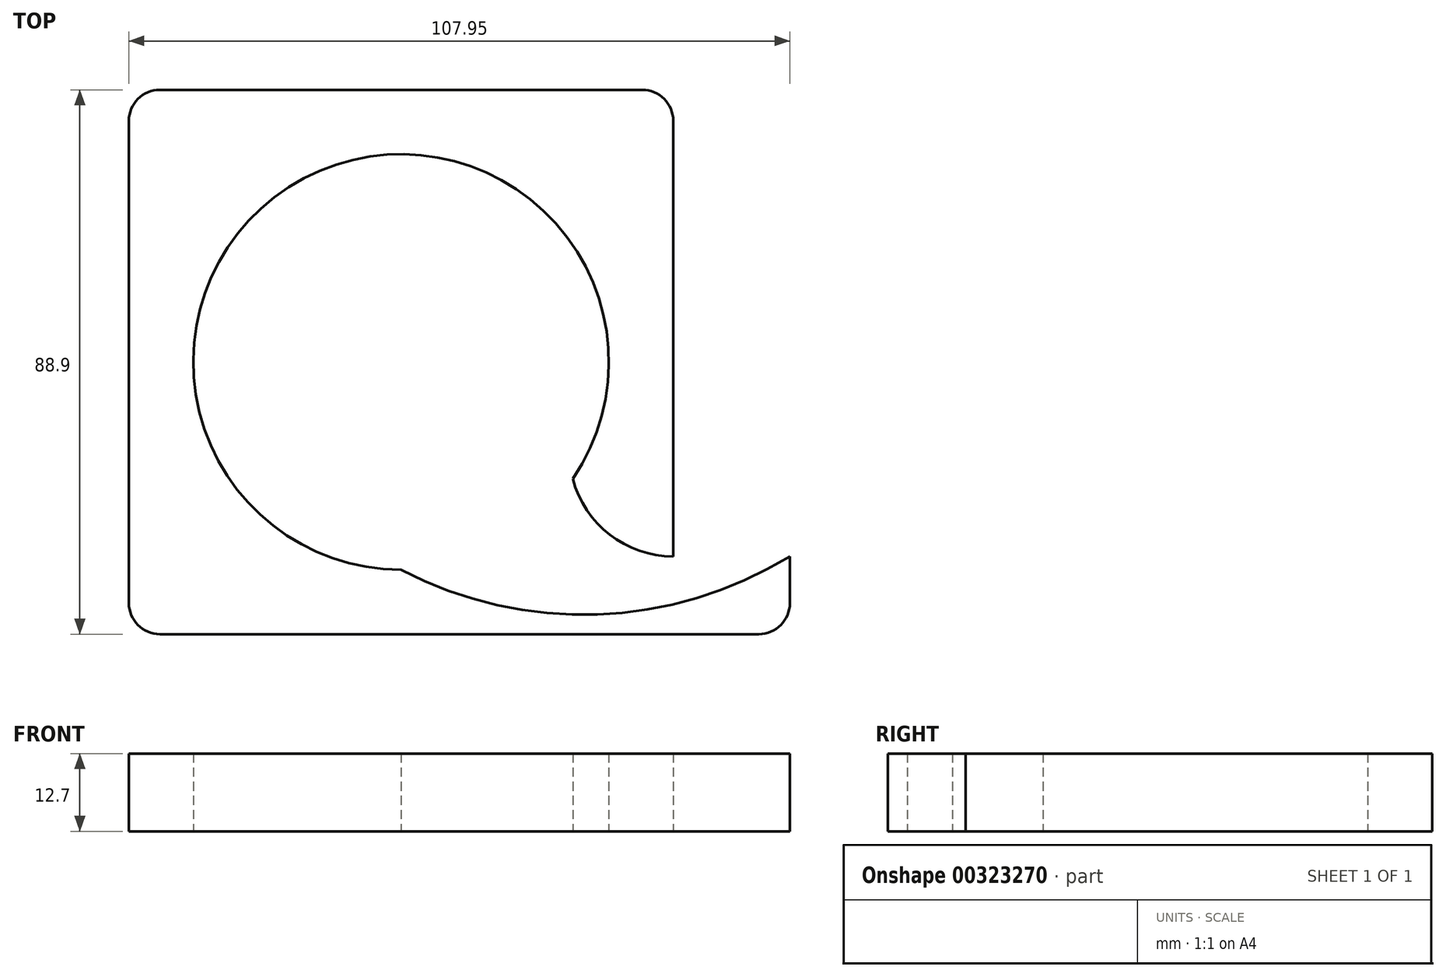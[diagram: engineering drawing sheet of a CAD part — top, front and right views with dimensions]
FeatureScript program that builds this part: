
annotation { "Feature Type Name" : "Feature", "Feature Type Description" : "" }
export const myFeature = defineFeature(function(context is Context, id is Id, definition is map)
    precondition{}
    {
        {
            var Q0;
            Q0=qCreatedBy(makeId("Top.planeOp"),FACE);
            var sketch = newSketch(context, id + "F0", { "sketchPlane" : qUnion([Q0])});
            skLineSegment(sketch, "E0.bottom", {"start": v(-44.45, 44.45) * mm, "end": v(44.45, 44.45) * mm});
            skLineSegment(sketch, "E0.top", {"start": v(-44.45, -44.45) * mm, "end": v(44.45, -44.45) * mm});
            skLineSegment(sketch, "E0.left", {"start": v(-44.45, 44.45) * mm, "end": v(-44.45, -44.45) * mm});
            skLineSegment(sketch, "E0.right", {"start": v(44.45, 44.45) * mm, "end": v(44.45, -31.75) * mm});
            skPoint(sketch, "E0.middle", {"position": v(0, 0) * mm});
            skLineSegment(sketch, "E1.bottom", {"start": v(44.45, -44.45) * mm, "end": v(63.5, -44.45) * mm});
            skLineSegment(sketch, "E1.right", {"start": v(63.5, -44.45) * mm, "end": v(63.5, -31.75) * mm});
            skArc(sketch, "E2", {"start": v(28.04, -19.1) * mm, "mid": v(-15.86, 30) * mm, "end": v(0, -33.93) * mm});
            skArc(sketch, "E3", {"start": v(0, -33.93) * mm, "mid": v(32.04, -41.23) * mm, "end": v(63.5, -31.75) * mm});
            skArc(sketch, "E4", {"start": v(28.04, -19.1) * mm, "mid": v(34.1, -28.22) * mm, "end": v(44.45, -31.75) * mm});
            skSolve(sketch);
        }
        {
            var Q0;
            Q0=makeQuery(id+"F0.imprint","IMPRINT",FACE,{"disambiguationData":[TD([[makeQuery(id+"F0.imprint","IMPRINT",EDGE,{"derivedFrom":sQuery(id+"F0.wireOp",EDGE,"E0.bottom")}),-1.0]])]});
            extrude(context, id + "F1", {"entities" : qUnion([Q0]), "depth" : 12.7 * mm});
        }
        {
            var Q0;
            Q0=makeQuery(id+"F1.opExtrude","SWEPT_EDGE",EDGE,{"disambiguationData":[OSD([sQuery(id+"F0.wireOp",EDGE,"E0.top"),sQuery(id+"F0.wireOp",EDGE,"E0.left")])]});
            var Q1;
            Q1=makeQuery(id+"F1.opExtrude","SWEPT_EDGE",EDGE,{"disambiguationData":[OSD([sQuery(id+"F0.wireOp",EDGE,"E1.bottom"),sQuery(id+"F0.wireOp",EDGE,"E1.right")])]});
            var Q2;
            Q2=makeQuery(id+"F1.opExtrude","SWEPT_EDGE",EDGE,{"disambiguationData":[OSD([sQuery(id+"F0.wireOp",EDGE,"E0.bottom"),sQuery(id+"F0.wireOp",EDGE,"E0.right")])]});
            var Q3;
            Q3=makeQuery(id+"F1.opExtrude","SWEPT_EDGE",EDGE,{"disambiguationData":[OSD([sQuery(id+"F0.wireOp",EDGE,"E0.bottom"),sQuery(id+"F0.wireOp",EDGE,"E0.left")])]});
            fillet(context, id + "F2", {"entities" : qUnion([Q0, Q1, Q2, Q3]), "radius" : 5.08 * mm, "tangentPropagation" : true, "allowEdgeOverflow" : false});
        }
    });
